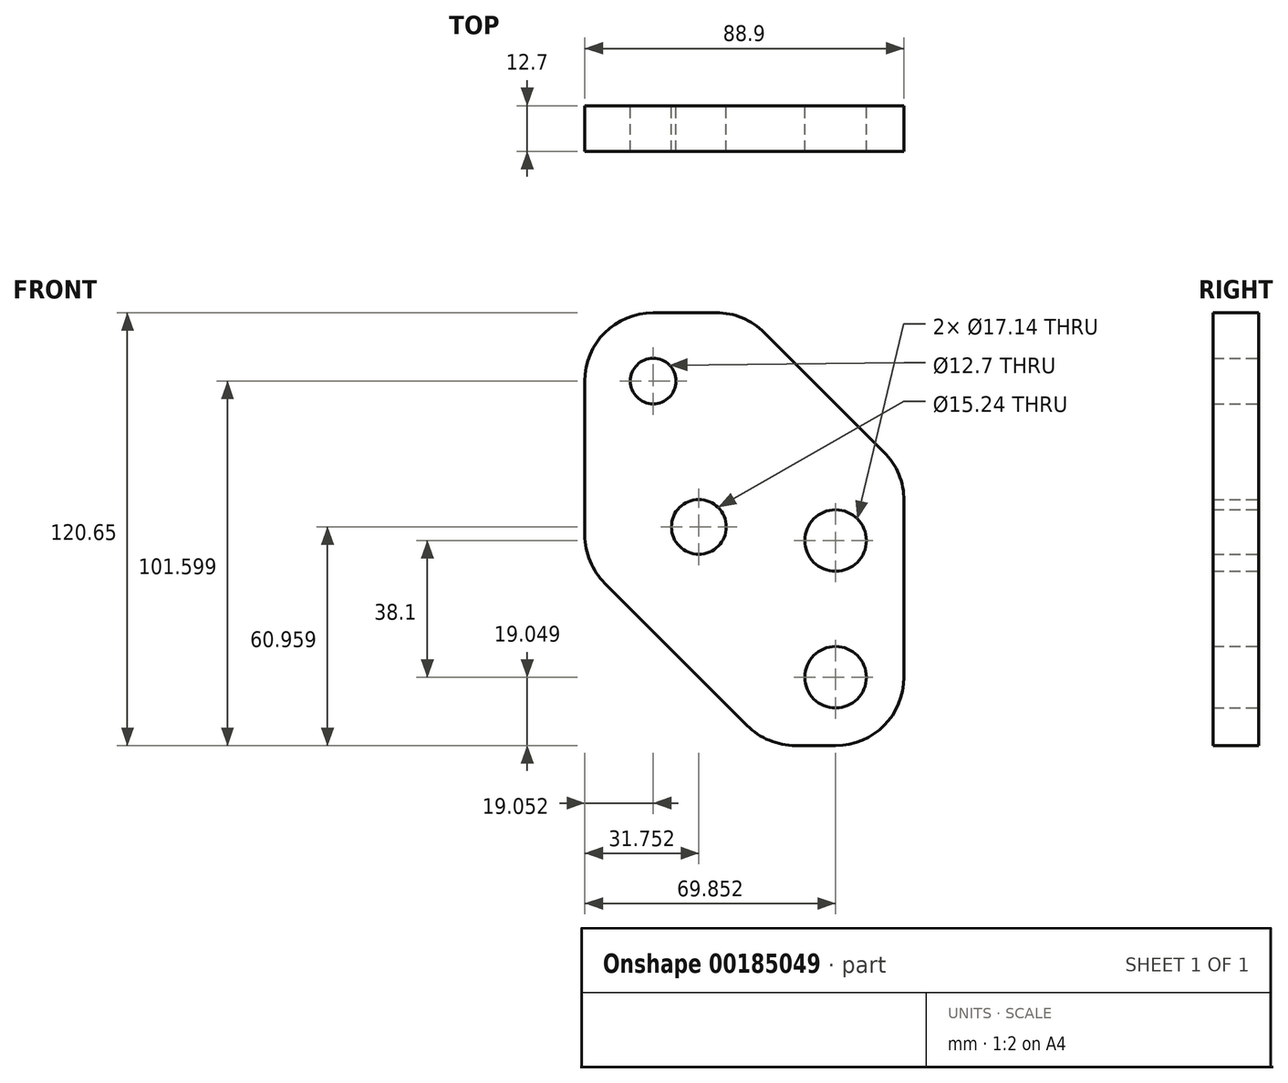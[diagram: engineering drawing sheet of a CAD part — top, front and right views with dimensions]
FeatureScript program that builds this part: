
annotation { "Feature Type Name" : "Feature", "Feature Type Description" : "" }
export const myFeature = defineFeature(function(context is Context, id is Id, definition is map)
    precondition{}
    {
        {
            var Q0;
            Q0=qCreatedBy(makeId("Front.planeOp"),FACE);
            var sketch = newSketch(context, id + "F0", { "sketchPlane" : qUnion([Q0])});
            skLineSegment(sketch, "E0.bottom", {"start": v(-38.03, -29.1) * mm, "end": v(-49.19, -29.1) * mm});
            skLineSegment(sketch, "E0.left", {"start": v(-18.98, -10.05) * mm, "end": v(-18.98, 39.2) * mm});
            skLineSegment(sketch, "E0.right", {"start": v(-107.88, 29.59) * mm, "end": v(-107.88, 47.1) * mm});
            skLineSegment(sketch, "E1", {"start": v(-62.66, -23.52) * mm, "end": v(-102.3, 16.12) * mm});
            skLineSegment(sketch, "E2", {"start": v(-38.03, -45.53) * mm, "end": v(-38.03, 70.95) * mm, "construction": true});
            skCircle(sketch, "E3", {"center": v(-38.03, -10.05) * mm, "radius": 8.57 * mm});
            skCircle(sketch, "E4", {"center": v(-38.03, 28.05) * mm, "radius": 8.57 * mm});
            skLineSegment(sketch, "E5", {"start": v(-107.88, 47.1) * mm, "end": v(-107.88, 72.5) * mm});
            skLineSegment(sketch, "E6", {"start": v(-88.83, 91.55) * mm, "end": v(-71.32, 91.55) * mm});
            skLineSegment(sketch, "E7", {"start": v(-57.85, 85.97) * mm, "end": v(-24.56, 52.68) * mm});
            skLineSegment(sketch, "E8", {"start": v(-120.53, 72.5) * mm, "end": v(-24.77, 72.5) * mm, "construction": true});
            skLineSegment(sketch, "E9", {"start": v(-88.83, 106.9) * mm, "end": v(-88.83, -11.48) * mm, "construction": true});
            skCircle(sketch, "E10", {"center": v(-88.83, 72.5) * mm, "radius": 6.35 * mm});
            skPoint(sketch, "E11.visualSharp", {"position": v(-107.88, 91.55) * mm});
            skArc(sketch, "E11.filletArc", {"start": v(-88.83, 91.55) * mm, "mid": v(-102.3, 85.97) * mm, "end": v(-107.88, 72.5) * mm});
            skPoint(sketch, "E12.visualSharp", {"position": v(-63.43, 91.55) * mm});
            skArc(sketch, "E12.filletArc", {"start": v(-57.85, 85.97) * mm, "mid": v(-64.03, 90.1) * mm, "end": v(-71.32, 91.55) * mm});
            skPoint(sketch, "E13.visualSharp", {"position": v(-18.98, 47.1) * mm});
            skArc(sketch, "E13.filletArc", {"start": v(-18.98, 39.2) * mm, "mid": v(-20.43, 46.5) * mm, "end": v(-24.56, 52.68) * mm});
            skPoint(sketch, "E14.visualSharp", {"position": v(-107.88, 21.7) * mm});
            skArc(sketch, "E14.filletArc", {"start": v(-107.88, 29.59) * mm, "mid": v(-106.43, 22.3) * mm, "end": v(-102.3, 16.12) * mm});
            skPoint(sketch, "E15.visualSharp", {"position": v(-57.08, -29.1) * mm});
            skArc(sketch, "E15.filletArc", {"start": v(-62.66, -23.52) * mm, "mid": v(-56.48, -27.65) * mm, "end": v(-49.19, -29.1) * mm});
            skPoint(sketch, "E16.visualSharp", {"position": v(-18.98, -29.1) * mm});
            skArc(sketch, "E16.filletArc", {"start": v(-38.03, -29.1) * mm, "mid": v(-24.56, -23.52) * mm, "end": v(-18.98, -10.05) * mm});
            skLineSegment(sketch, "E17", {"start": v(-107.88, 47.1) * mm, "end": v(-76.13, 47.1) * mm, "construction": true});
            skLineSegment(sketch, "E18", {"start": v(-76.13, 31.86) * mm, "end": v(-76.13, 47.1) * mm, "construction": true});
            skCircle(sketch, "E19", {"center": v(-76.13, 31.86) * mm, "radius": 7.62 * mm});
            skSolve(sketch);
        }
        {
            var Q0;
            Q0=makeQuery(id+"F0.imprint","IMPRINT",FACE,{"disambiguationData":[TD([[makeQuery(id+"F0.imprint","IMPRINT",EDGE,{"derivedFrom":sQuery(id+"F0.wireOp",EDGE,"E0.bottom")}),-1.0]])]});
            extrude(context, id + "F1", {"entities" : qUnion([Q0]), "depth" : 12.7 * mm});
        }
    });
